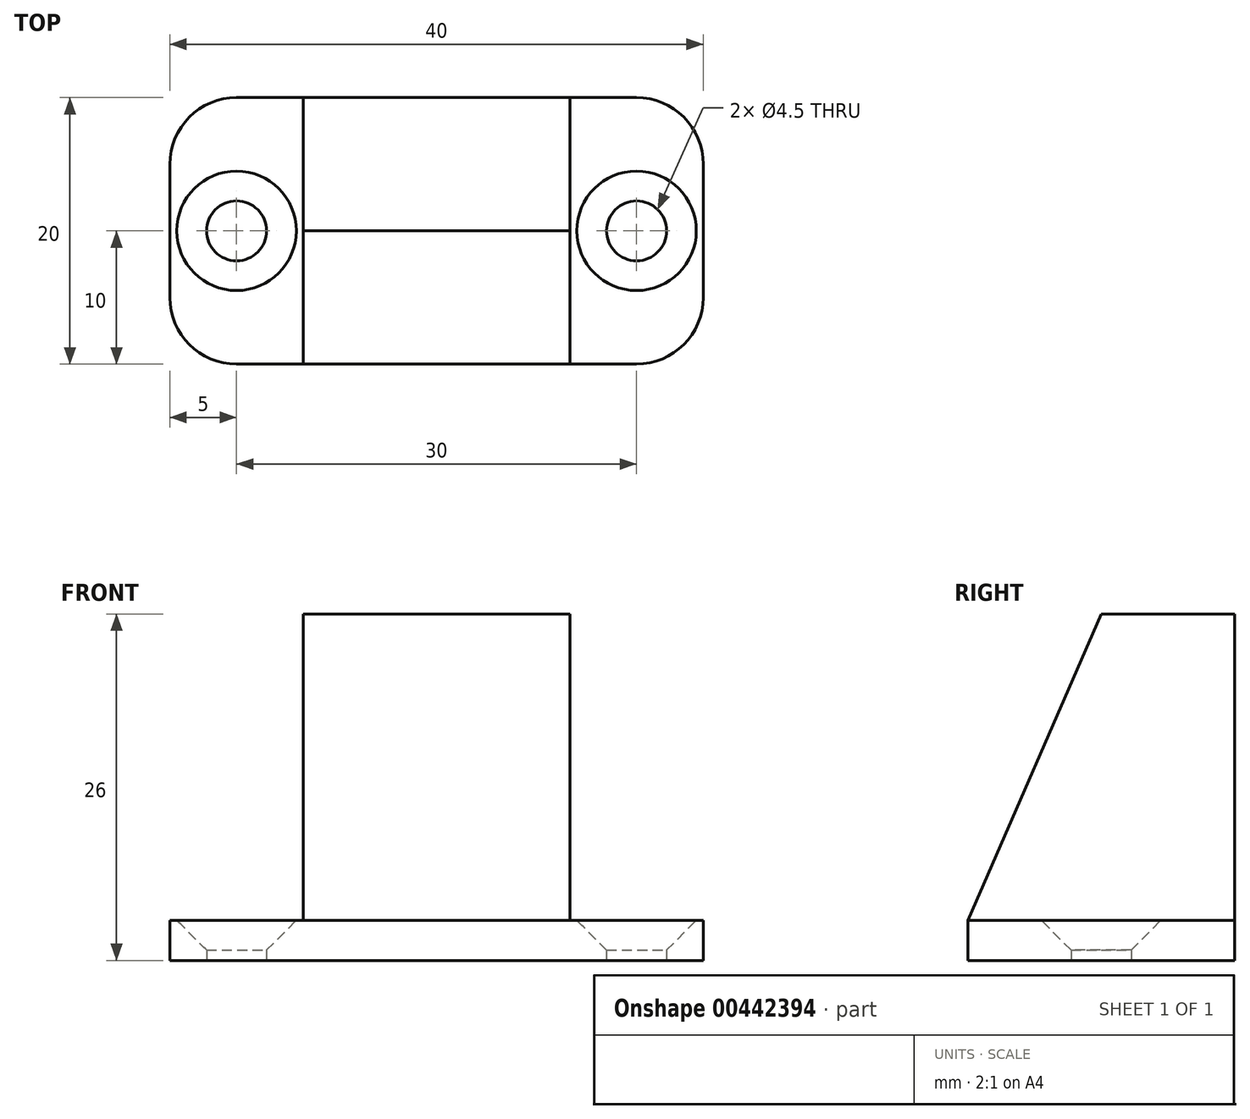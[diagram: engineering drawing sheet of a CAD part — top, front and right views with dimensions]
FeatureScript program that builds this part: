
annotation { "Feature Type Name" : "Feature", "Feature Type Description" : "" }
export const myFeature = defineFeature(function(context is Context, id is Id, definition is map)
    precondition{}
    {
        {
            var Q0;
            Q0=qCreatedBy(makeId("Front.planeOp"),FACE);
            var sketch = newSketch(context, id + "F0", { "sketchPlane" : qUnion([Q0])});
            skLineSegment(sketch, "E0.bottom", {"start": v(-10, 0) * mm, "end": v(10, 0) * mm});
            skLineSegment(sketch, "E0.top", {"start": v(-10, 23) * mm, "end": v(10, 23) * mm});
            skLineSegment(sketch, "E0.left", {"start": v(-10, 0) * mm, "end": v(-10, 23) * mm});
            skLineSegment(sketch, "E0.right", {"start": v(10, 0) * mm, "end": v(10, 23) * mm});
            skLineSegment(sketch, "E1.bottom", {"start": v(-20, 0) * mm, "end": v(20, 0) * mm});
            skLineSegment(sketch, "E1.top", {"start": v(-20, -3) * mm, "end": v(20, -3) * mm});
            skLineSegment(sketch, "E1.left", {"start": v(-20, 0) * mm, "end": v(-20, -3) * mm});
            skLineSegment(sketch, "E1.right", {"start": v(20, 0) * mm, "end": v(20, -3) * mm});
            skSolve(sketch);
        }
        {
            var Q0;
            Q0 = qSketchRegion(id + "F0", true);
            extrude(context, id + "F1", {"entities" : qUnion([Q0]), "depth" : 20 * mm, "offsetDistance" : 25 * mm});
        }
        {
            var Q0;
            Q0=makeQuery(id+"F1.opExtrude","CAP_EDGE",EDGE,{"disambiguationData":[OSD([sQuery(id+"F0.wireOp",EDGE,"E0.top")])],"isStart":false});
            chamfer(context, id + "F2", {"entities" : qUnion([Q0]), "chamferType" : ChamferType.TWO_OFFSETS, "width1" : 10 * mm, "oppositeDirection" : false, "width2" : 23 * mm, "tangentPropagation" : true});
        }
        {
            var Q0;
            {var subQ0=sQuery(id+"F0.wireOp",EDGE,"E1.bottom");Q0=makeQuery(id+"F1.opExtrude","SWEPT_FACE",FACE,{"disambiguationData":[OSD([subQ0]),TDD([makeQuery(id+"F0.imprint","IMPRINT",EDGE,{"disambiguationData":[TD([[makeQuery(id+"F0.imprint","INTERSECT",VERTEX,{"derivedFrom":[sQuery(id+"F0.wireOp",EDGE,"E0.left"),subQ0]}),1.0]])],"derivedFrom":subQ0})])]});}
            var sketch = newSketch(context, id + "F3", { "sketchPlane" : qUnion([Q0])});
            skPoint(sketch, "E2", {"position": v(-15, -10) * mm});
            skPoint(sketch, "E2.positionSnap0", {"position": v(-20, -10) * mm});
            skPoint(sketch, "E2.positionSnap1", {"position": v(-15, 0) * mm});
            skPoint(sketch, "E3.MirrorP", {"position": v(15, -10) * mm});
            skSolve(sketch);
        }
        {
            var Q0;
            Q0=sQuery(id+"F3.wireOp",VERTEX,"E2");
            var Q1;
            Q1=sQuery(id+"F3.wireOp",VERTEX,"E3.MirrorP");
            var Q2;
            Q2=makeQuery(id+"F1.opExtrude","SWEPT_BODY",BODY,{"disambiguationData":[OSD([sQuery(id+"F0.wireOp",EDGE,"E0.top"),sQuery(id+"F0.wireOp",EDGE,"E0.left"),sQuery(id+"F0.wireOp",EDGE,"E0.right"),sQuery(id+"F0.wireOp",EDGE,"E1.bottom"),sQuery(id+"F0.wireOp",EDGE,"E1.top"),sQuery(id+"F0.wireOp",EDGE,"E1.left"),sQuery(id+"F0.wireOp",EDGE,"E1.right")])]});
            hole(context, id + "F4", {"style" : HoleStyle.C_SINK, "endStyle" : HoleEndStyle.BLIND, "standardTappedOrClearance" : lookupTablePath({ "fit" : "Normal", "standard" : "ISO", "size" : "M4", "type" : "Clearance" }), "standardBlindInLast" : lookupTablePath({ "fit" : "Normal", "standard" : "ISO", "size" : "M4", "type" : "Clearance" }), "holeDiameter" : 4.5 * mm, "cSinkDiameter" : 8.96 * mm, "cSinkAngle" : 90 * degree, "majorDiameter" : 5 * mm, "holeDepth" : 12 * mm, "isTappedThrough" : true, "tappedDepth" : 12 * mm, "tapClearance" : 3, "locations" : qUnion([Q0, Q1]), "scope" : qUnion([Q2])});
        }
        {
            var Q0;
            Q0=makeQuery(id+"F1.opExtrude","CAP_EDGE",EDGE,{"disambiguationData":[OSD([sQuery(id+"F0.wireOp",EDGE,"E1.left")])],"isStart":false});
            var Q1;
            Q1=makeQuery(id+"F1.opExtrude","CAP_EDGE",EDGE,{"disambiguationData":[OSD([sQuery(id+"F0.wireOp",EDGE,"E1.right")])],"isStart":false});
            var Q2;
            Q2=makeQuery(id+"F1.opExtrude","CAP_EDGE",EDGE,{"disambiguationData":[OSD([sQuery(id+"F0.wireOp",EDGE,"E1.left")])],"isStart":true});
            var Q3;
            Q3=makeQuery(id+"F1.opExtrude","CAP_EDGE",EDGE,{"disambiguationData":[OSD([sQuery(id+"F0.wireOp",EDGE,"E1.right")])],"isStart":true});
            fillet(context, id + "F5", {"entities" : qUnion([Q0, Q1, Q2, Q3]), "radius" : 5 * mm, "tangentPropagation" : true, "allowEdgeOverflow" : false});
        }
    });
